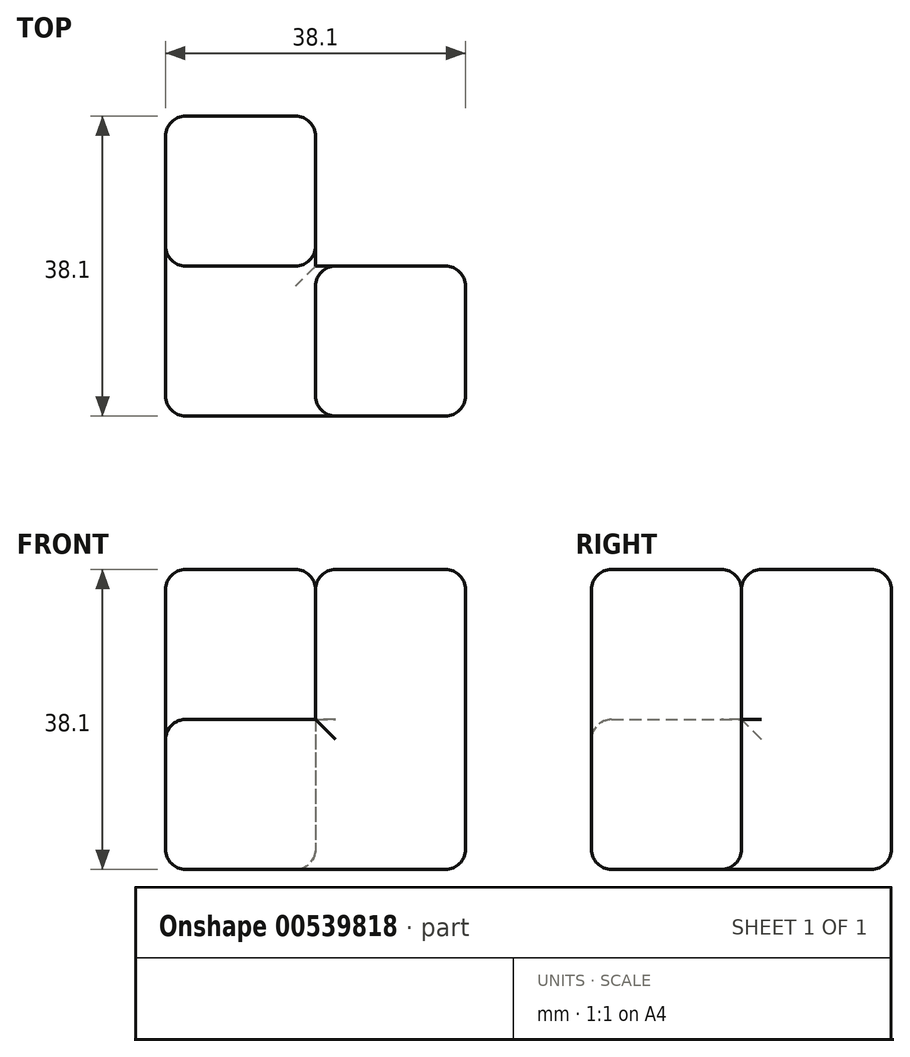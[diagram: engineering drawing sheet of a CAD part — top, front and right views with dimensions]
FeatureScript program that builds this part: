
annotation { "Feature Type Name" : "Feature", "Feature Type Description" : "" }
export const myFeature = defineFeature(function(context is Context, id is Id, definition is map)
    precondition{}
    {
        {
            var Q0;
            Q0=qCreatedBy(makeId("Top.planeOp"),FACE);
            var sketch = newSketch(context, id + "F0", { "sketchPlane" : qUnion([Q0])});
            skLineSegment(sketch, "E0", {"start": v(0, 0) * mm, "end": v(0, 38.1) * mm});
            skLineSegment(sketch, "E1", {"start": v(0, 38.1) * mm, "end": v(19.05, 38.1) * mm});
            skLineSegment(sketch, "E2", {"start": v(19.05, 38.1) * mm, "end": v(19.05, 19.05) * mm});
            skLineSegment(sketch, "E3", {"start": v(19.05, 19.05) * mm, "end": v(38.1, 19.05) * mm});
            skLineSegment(sketch, "E4", {"start": v(38.1, 19.05) * mm, "end": v(38.1, 0) * mm});
            skLineSegment(sketch, "E5", {"start": v(38.1, 0) * mm, "end": v(0, 0) * mm});
            skSolve(sketch);
        }
        {
            var Q0;
            Q0 = qSketchRegion(id + "F0", true);
            extrude(context, id + "F1", {"entities" : qUnion([Q0]), "depth" : 19.05 * mm, "offsetDistance" : 25.4 * mm});
        }
        {
            var Q0;
            Q0=makeQuery(id+"F1.opExtrude","CAP_FACE",FACE,{"disambiguationData":[OSD([sQuery(id+"F0.wireOp",EDGE,"E0"),sQuery(id+"F0.wireOp",EDGE,"E1"),sQuery(id+"F0.wireOp",EDGE,"E2"),sQuery(id+"F0.wireOp",EDGE,"E3"),sQuery(id+"F0.wireOp",EDGE,"E4"),sQuery(id+"F0.wireOp",EDGE,"E5")])],"isStart":false});
            var sketch = newSketch(context, id + "F2", { "sketchPlane" : qUnion([Q0])});
            skLineSegment(sketch, "E6.bottom", {"start": v(0, 38.1) * mm, "end": v(19.05, 38.1) * mm});
            skLineSegment(sketch, "E6.top", {"start": v(0, 19.05) * mm, "end": v(19.05, 19.05) * mm});
            skLineSegment(sketch, "E6.left", {"start": v(0, 38.1) * mm, "end": v(0, 19.05) * mm});
            skLineSegment(sketch, "E6.right", {"start": v(19.05, 38.1) * mm, "end": v(19.05, 19.05) * mm});
            skLineSegment(sketch, "E7.bottom", {"start": v(38.1, 0) * mm, "end": v(19.05, 0) * mm});
            skLineSegment(sketch, "E7.top", {"start": v(38.1, 19.05) * mm, "end": v(19.05, 19.05) * mm});
            skLineSegment(sketch, "E7.left", {"start": v(38.1, 0) * mm, "end": v(38.1, 19.05) * mm});
            skLineSegment(sketch, "E7.right", {"start": v(19.05, 0) * mm, "end": v(19.05, 19.05) * mm});
            skSolve(sketch);
        }
        {
            var Q0;
            Q0=makeQuery(id+"F2.imprint","IMPRINT",FACE,{"disambiguationData":[TD([[makeQuery(id+"F2.imprint","IMPRINT",EDGE,{"derivedFrom":sQuery(id+"F2.wireOp",EDGE,"E7.bottom")}),-1.0]])]});
            extrude(context, id + "F3", {"entities" : qUnion([Q0]), "operationType" : NewBodyOperationType.ADD, "depth" : 19.05 * mm, "offsetDistance" : 25.4 * mm});
        }
        {
            var Q0;
            Q0=makeQuery(id+"F3.opExtrude","SWEPT_EDGE",EDGE,{"disambiguationData":[OSD([sQuery(id+"F2.wireOp",EDGE,"E6.top"),sQuery(id+"F2.wireOp",EDGE,"E6.right"),sQuery(id+"F2.wireOp",EDGE,"E7.top"),sQuery(id+"F2.wireOp",EDGE,"E7.right")])]});
            fillet(context, id + "F4", {"entities" : qUnion([Q0]), "radius" : 2.54 * mm, "tangentPropagation" : true, "allowEdgeOverflow" : false});
        }
        {
            var Q0;
            Q0=makeQuery(id+"F2.imprint","IMPRINT",FACE,{"disambiguationData":[TD([[makeQuery(id+"F2.imprint","IMPRINT",EDGE,{"derivedFrom":sQuery(id+"F2.wireOp",EDGE,"E6.bottom")}),-1.0]])]});
            extrude(context, id + "F5", {"entities" : qUnion([Q0]), "operationType" : NewBodyOperationType.ADD, "depth" : 19.05 * mm, "offsetDistance" : 25.4 * mm});
        }
        {
            var Q0;
            Q0=makeQuery(id+"F3.boolean.opBoolean","MERGE",FACE,{"derivedFrom":[makeQuery(id+"F1.opExtrude","SWEPT_FACE",FACE,{"disambiguationData":[OSD([sQuery(id+"F0.wireOp",EDGE,"E4")])]}),makeQuery(id+"F3.opExtrude","SWEPT_FACE",FACE,{"disambiguationData":[OSD([sQuery(id+"F2.wireOp",EDGE,"E7.left")])]})]});
            var Q1;
            Q1=makeQuery(id+"F5.boolean.opBoolean","MERGE",FACE,{"derivedFrom":[makeQuery(id+"F1.opExtrude","SWEPT_FACE",FACE,{"disambiguationData":[OSD([sQuery(id+"F0.wireOp",EDGE,"E1")])]}),makeQuery(id+"F5.opExtrude","SWEPT_FACE",FACE,{"disambiguationData":[OSD([sQuery(id+"F2.wireOp",EDGE,"E6.bottom")])]})]});
            var Q2;
            Q2=makeQuery(id+"F5.opExtrude","CAP_FACE",FACE,{"disambiguationData":[OSD([sQuery(id+"F2.wireOp",EDGE,"E6.bottom"),sQuery(id+"F2.wireOp",EDGE,"E6.top"),sQuery(id+"F2.wireOp",EDGE,"E6.left"),sQuery(id+"F2.wireOp",EDGE,"E6.right")])],"isStart":false});
            var Q3;
            Q3=makeQuery(id+"F3.opExtrude","CAP_FACE",FACE,{"disambiguationData":[OSD([sQuery(id+"F2.wireOp",EDGE,"E7.bottom"),sQuery(id+"F2.wireOp",EDGE,"E7.top"),sQuery(id+"F2.wireOp",EDGE,"E7.left"),sQuery(id+"F2.wireOp",EDGE,"E7.right")])],"isStart":false});
            var Q4;
            Q4=makeQuery(id+"F5.boolean.opBoolean","MERGE",FACE,{"derivedFrom":[makeQuery(id+"F1.opExtrude","SWEPT_FACE",FACE,{"disambiguationData":[OSD([sQuery(id+"F0.wireOp",EDGE,"E0")])]}),makeQuery(id+"F5.opExtrude","SWEPT_FACE",FACE,{"disambiguationData":[OSD([sQuery(id+"F2.wireOp",EDGE,"E6.left")])]})]});
            var Q5;
            Q5=makeQuery(id+"F3.boolean.opBoolean","MERGE",FACE,{"derivedFrom":[makeQuery(id+"F1.opExtrude","SWEPT_FACE",FACE,{"disambiguationData":[OSD([sQuery(id+"F0.wireOp",EDGE,"E5")])]}),makeQuery(id+"F3.opExtrude","SWEPT_FACE",FACE,{"disambiguationData":[OSD([sQuery(id+"F2.wireOp",EDGE,"E7.bottom")])]})]});
            var Q6;
            Q6=makeQuery(id+"F1.opExtrude","CAP_FACE",FACE,{"disambiguationData":[OSD([sQuery(id+"F0.wireOp",EDGE,"E0"),sQuery(id+"F0.wireOp",EDGE,"E1"),sQuery(id+"F0.wireOp",EDGE,"E2"),sQuery(id+"F0.wireOp",EDGE,"E3"),sQuery(id+"F0.wireOp",EDGE,"E4"),sQuery(id+"F0.wireOp",EDGE,"E5")])],"isStart":true});
            var Q7;
            Q7=makeQuery(id+"F5.opExtrude","SWEPT_EDGE",EDGE,{"disambiguationData":[OSD([sQuery(id+"F2.wireOp",EDGE,"E6.top"),sQuery(id+"F2.wireOp",EDGE,"E6.right"),sQuery(id+"F2.wireOp",EDGE,"E7.top"),sQuery(id+"F2.wireOp",EDGE,"E7.right")])]});
            fillet(context, id + "F6", {"entities" : qUnion([Q0, Q1, Q2, Q3, Q4, Q5, Q6, Q7]), "radius" : 2.54 * mm, "tangentPropagation" : true, "allowEdgeOverflow" : false});
        }
    });
